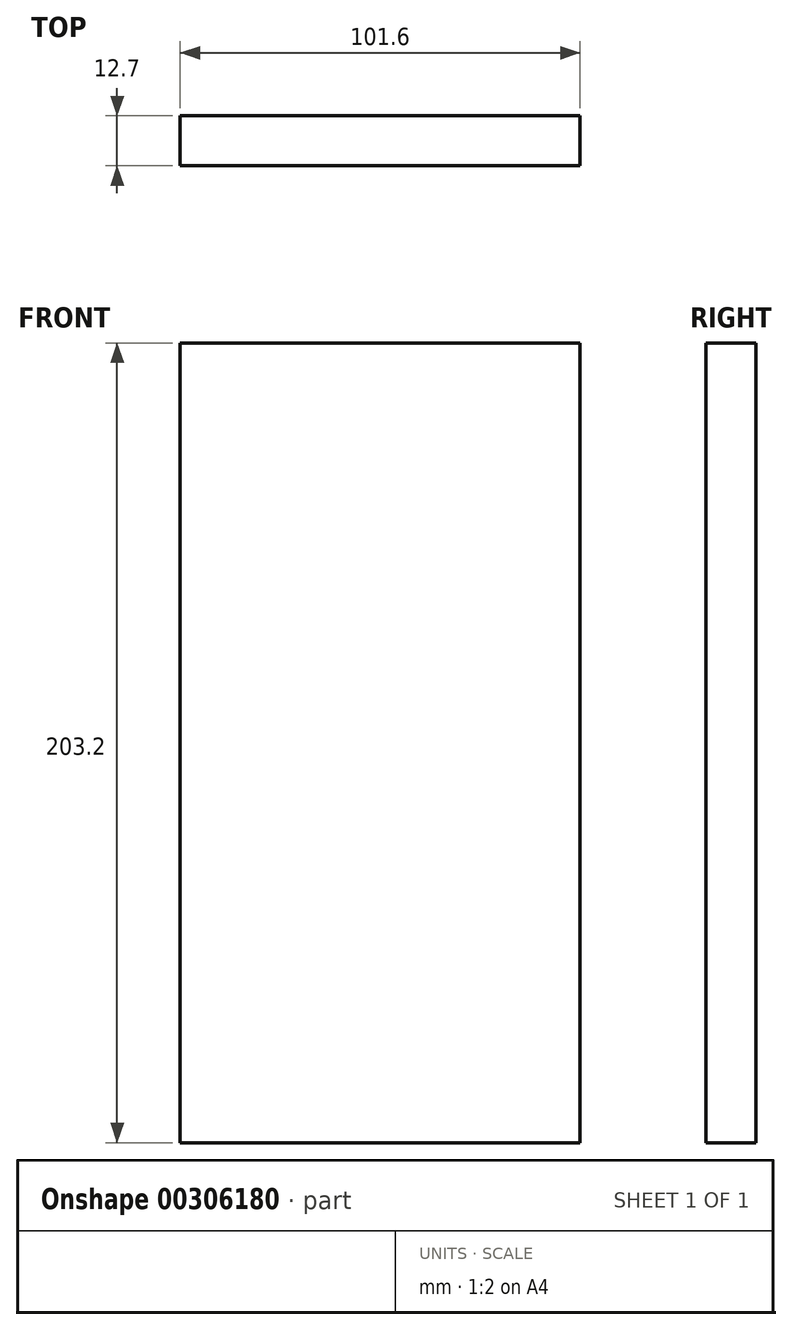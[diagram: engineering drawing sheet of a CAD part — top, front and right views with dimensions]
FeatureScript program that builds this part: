
annotation { "Feature Type Name" : "Feature", "Feature Type Description" : "" }
export const myFeature = defineFeature(function(context is Context, id is Id, definition is map)
    precondition{}
    {
        {
            var Q0;
            Q0=qCreatedBy(makeId("Front.planeOp"),FACE);
            var sketch = newSketch(context, id + "F0", { "sketchPlane" : qUnion([Q0])});
            skLineSegment(sketch, "E0.bottom", {"start": v(50.8, -101.6) * mm, "end": v(-50.8, -101.6) * mm});
            skLineSegment(sketch, "E0.top", {"start": v(50.8, 101.6) * mm, "end": v(-50.8, 101.6) * mm});
            skLineSegment(sketch, "E0.left", {"start": v(50.8, -101.6) * mm, "end": v(50.8, 101.6) * mm});
            skLineSegment(sketch, "E0.right", {"start": v(-50.8, -101.6) * mm, "end": v(-50.8, 101.6) * mm});
            skPoint(sketch, "E0.middle", {"position": v(0, 0) * mm});
            skSolve(sketch);
        }
        {
            var Q0;
            Q0 = qSketchRegion(id + "F0", true);
            extrude(context, id + "F1", {"entities" : qUnion([Q0]), "depth" : 12.7 * mm});
        }
    });
